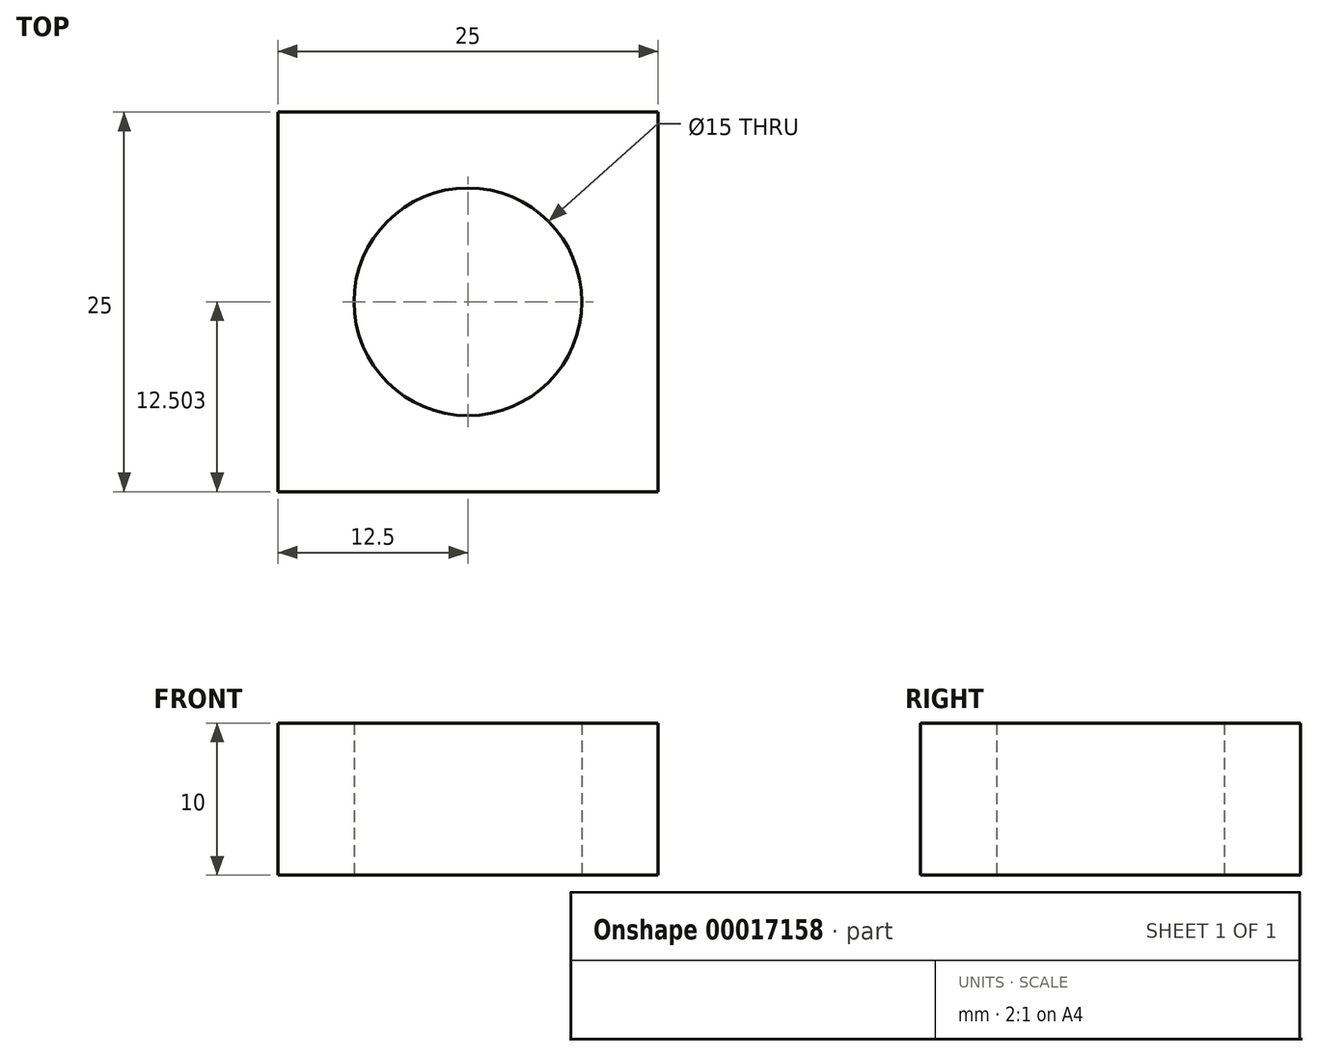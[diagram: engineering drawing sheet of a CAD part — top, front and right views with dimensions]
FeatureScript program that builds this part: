
annotation { "Feature Type Name" : "Feature", "Feature Type Description" : "" }
export const myFeature = defineFeature(function(context is Context, id is Id, definition is map)
    precondition{}
    {
        {
            var Q0;
            Q0=qCreatedBy(makeId("Top.planeOp"),FACE);
            var sketch = newSketch(context, id + "F0", { "sketchPlane" : qUnion([Q0])});
            skLineSegment(sketch, "E0.bottom", {"start": v(-12.5, 18.28) * mm, "end": v(12.5, 18.28) * mm});
            skLineSegment(sketch, "E0.top", {"start": v(-12.5, -6.72) * mm, "end": v(12.5, -6.72) * mm});
            skLineSegment(sketch, "E0.left", {"start": v(-12.5, 18.28) * mm, "end": v(-12.5, -6.72) * mm});
            skLineSegment(sketch, "E0.right", {"start": v(12.5, 18.28) * mm, "end": v(12.5, -6.72) * mm});
            skLineSegment(sketch, "E1", {"start": v(-12.5, 5.78) * mm, "end": v(12.5, 5.78) * mm});
            skCircle(sketch, "E2", {"center": v(0, 5.78) * mm, "radius": 7.5 * mm});
            skSolve(sketch);
        }
        {
            var Q0;
            Q0 = qSketchRegion(id + "F0", true);
            extrude(context, id + "F1", {"entities" : qUnion([Q0]), "depth" : 10 * mm});
        }
    });
